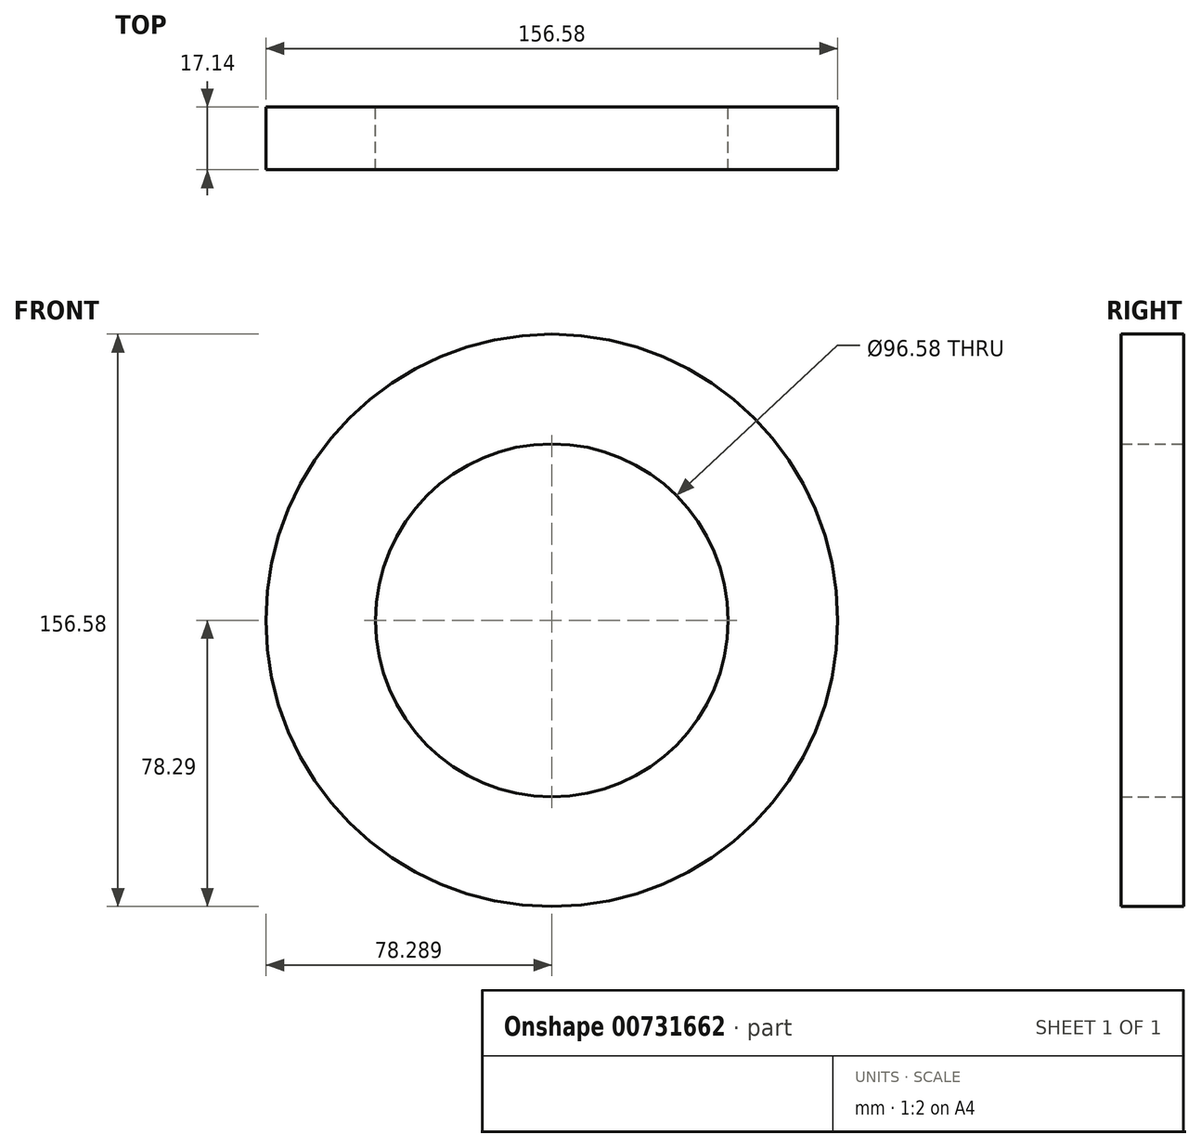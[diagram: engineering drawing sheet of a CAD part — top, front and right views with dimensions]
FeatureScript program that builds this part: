
annotation { "Feature Type Name" : "Feature", "Feature Type Description" : "" }
export const myFeature = defineFeature(function(context is Context, id is Id, definition is map)
    precondition{}
    {
        {
            var Q0;
            Q0=qCreatedBy(makeId("Top.planeOp"),FACE);
            var sketch = newSketch(context, id + "F0", { "sketchPlane" : qUnion([Q0])});
            skLineSegment(sketch, "E0.bottom", {"start": v(15, 8.57) * mm, "end": v(-15, 8.57) * mm});
            skLineSegment(sketch, "E0.top", {"start": v(15, -8.57) * mm, "end": v(-15, -8.57) * mm});
            skLineSegment(sketch, "E0.left", {"start": v(15, 8.57) * mm, "end": v(15, -8.57) * mm});
            skLineSegment(sketch, "E0.right", {"start": v(-15, 8.57) * mm, "end": v(-15, -8.57) * mm});
            skPoint(sketch, "E0.middle", {"position": v(0, 0) * mm});
            skSolve(sketch);
        }
        {
            var Q0;
            Q0=qCreatedBy(makeId("Top.planeOp"),FACE);
            var sketch = newSketch(context, id + "F1", { "sketchPlane" : qUnion([Q0])});
            skLineSegment(sketch, "E1", {"start": v(63.29, 83.3) * mm, "end": v(63.29, -80.75) * mm, "construction": true});
            skSolve(sketch);
        }
        {
            var Q0;
            Q0 = qSketchRegion(id + "F0", true);
            var Q1;
            Q1=sQuery(id+"F1.wireOp",EDGE,"E1");
            revolve(context, id + "F2", {"surfaceOperationType" : NewSurfaceOperationType.NEW, "entities" : qUnion([Q0]), "axis" : qUnion([Q1]), "revolveType" : RevolveType.FULL});
        }
    });
